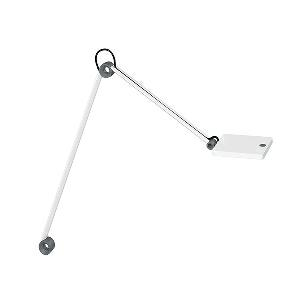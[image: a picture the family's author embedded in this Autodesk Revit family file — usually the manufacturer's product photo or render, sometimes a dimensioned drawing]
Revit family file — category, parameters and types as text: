
# Revit family: para_mi_-_ftl_108_r__930_00632662_8d9b
name_source: partatom
category: Lighting Fixtures
units: mm (PartAtom-declared; Revit-internal decimal feet)

## family parameters
Cut with Voids When Loaded = No
Host = Face
Light Source = No
Part Type = Normal
Room Calculation Point = No
Round Connector Dimension = Use Diameter
Shared = No

## types (1)
- PARA.MI - FTL 108 R /930 (1 x LED, 580 lm, 3000K)
    Apparent Load = 7 VA
    Approval mark = CE
    CIE Flux Codes = 70 94 99 100 100
    Color Rendering = 90-100
    Color Temperature = 3000K
    Control Gear = Electronic ballast
    Default Elevation = 1800 mm
    Description = FTL 108 R|Task luminaire|light source: LED|work equipment: Electronic plug-in transformer|connected load: 100-240 V, 50/60 Hz|Power consumption: approx. 7 W|luminous flux: 580 lm|luminous efficacy: 82 lm/W|Illuminance efficiency factor: 107 lx/W|colour temperature: Warm white, ca. 3000 K|color rendering index (CRI): >= 90|chromaticity tolerance:  3 SDCM|class of protection: II with plug-in power supply, III without plug-in power supply|technology: Continuously dimmable|luminaire body|material: Aluminium|surface: Painted|colour: White|lamp cover: Plastic, Clear|tubular sections|material: Tubular aluminium section|surface: Painted|colour: White|weight (net): approx. 1.0 kg|mains lead: 3.00 m Mains plug BS 1363, CEE 7/XVI, NEMA 1-15P|Fastening: Adaptor (accessory), Table base (accessory), Table clamp (accessory), Tap16|glare control: Reflector|special features: Automatic switchoff adjustable, Push button in luminaire head, Behaviour at net recovery adjustable|Approval mark: C - ETL - US (F. CAN U. USA), VDE - ENEC SEP LIGHT & POWER SUPPLY UNIT|
    Height = 12 mm  [stored 0.0393701 ft]
    Lamp = 1 x LED
    Lamp Light Flux = 580 lm
    Lamp count = 1
    Length = 123 mm
    Luminous efficacy = 83 lm/W
    Manufacturer = Waldmann
    ModVariant = No
    Model = 00632662
    Mounting Place = Table
    Mounting Type = Surface mounted
    Number of Poles = 1
    OnlyDefault = Yes
    Power Factor = 1
    Product Name = PARA.MI - FTL 108 R /930
    Product group = Task luminaire (office)
    ProductGroupID = 21
    Protection Class = Protection class II
    Protection Degree = IP 40
    RLX_Detail_Level = 1
    RLX_Emergency_Light_Flux = 0 lm
    RLX_Emergency_Type = 0
    RLX_Emergency_Type_DB = No
    RlxData = <blob elided: 68609 chars, md5=8a2a338f>
    Socket = socket
    Standby Power = 0 W
    System Light Flux = 580 lm
    System Power = 7 W
    Type Comments = Product without accessories
    Type Image = 113148000-00638510.jpg
    URL = http://relux.com
    VarID = ---
    Voltage = 230 V
    Voltage Range = 220-240 V
    Weight = 0.00 kg
    Width = 0 mm  [stored 0 ft]

note: [stored X ft] marks values corroborated as IEEE doubles in the binary element streams (Revit-internal decimal feet)

## geometry (parser evidence)
native form markers: Blend x4, Sweep x12
no freeform markers — native parametric forms only
